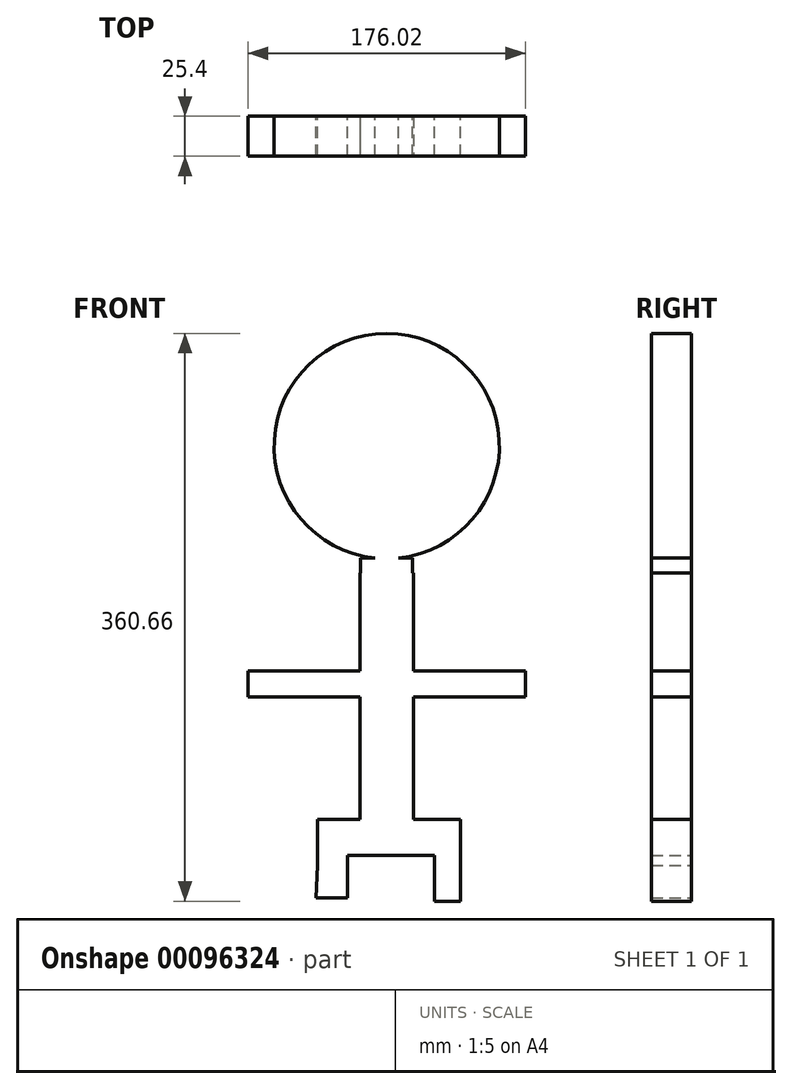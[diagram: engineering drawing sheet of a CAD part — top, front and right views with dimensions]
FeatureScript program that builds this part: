
annotation { "Feature Type Name" : "Feature", "Feature Type Description" : "" }
export const myFeature = defineFeature(function(context is Context, id is Id, definition is map)
    precondition{}
    {
        {
            var Q0;
            Q0=qCreatedBy(makeId("Front.planeOp"),FACE);
            var sketch = newSketch(context, id + "F0", { "sketchPlane" : qUnion([Q0])});
            skCircle(sketch, "E0", {"center": v(0, 0) * mm, "radius": 71.54 * mm});
            skSolve(sketch);
        }
        {
            var Q0;
            Q0=makeQuery(id+"F0.imprint","IMPRINT",FACE,{"disambiguationData":[TD([[makeQuery(id+"F0.imprint","IMPRINT",EDGE,{"derivedFrom":sQuery(id+"F0.wireOp",EDGE,"E0")}),1.0]])]});
            extrude(context, id + "F1", {"entities" : qUnion([Q0]), "depth" : 25.4 * mm});
        }
        {
            var Q0;
            Q0=qCreatedBy(makeId("Front.planeOp"),FACE);
            var sketch = newSketch(context, id + "F2", { "sketchPlane" : qUnion([Q0])});
            skCircle(sketch, "E1", {"center": v(-21.64, 37.84) * mm, "radius": 12.7 * mm});
            skCircle(sketch, "E2", {"center": v(21.64, 37.84) * mm, "radius": 12.7 * mm});
            skSolve(sketch);
        }
        {
            var Q0;
            Q0=sQuery(id+"F2.wireOp",EDGE,"E1");
            var Q1;
            Q1=sQuery(id+"F2.wireOp",EDGE,"E2");
            extrude(context, id + "F3", {"bodyType" : ToolBodyType.SURFACE, "surfaceEntities" : qUnion([Q0, Q1]), "depth" : 25.4 * mm});
        }
        {
            var Q0;
            Q0=qCreatedBy(makeId("Front.planeOp"),FACE);
            var sketch = newSketch(context, id + "F4", { "sketchPlane" : qUnion([Q0])});
            skLineSegment(sketch, "E3.bottom", {"start": v(0, -71.13) * mm, "end": v(-16.78, -71.13) * mm});
            skLineSegment(sketch, "E3.top", {"start": v(0, -145.62) * mm, "end": v(-16.78, -145.62) * mm});
            skLineSegment(sketch, "E3.left", {"start": v(0, -71.13) * mm, "end": v(0, -145.62) * mm});
            skLineSegment(sketch, "E3.right", {"start": v(-16.78, -71.13) * mm, "end": v(-16.78, -145.62) * mm});
            skLineSegment(sketch, "E4.bottom", {"start": v(0, -71.13) * mm, "end": v(16.43, -71.13) * mm});
            skLineSegment(sketch, "E4.top", {"start": v(0, -145.62) * mm, "end": v(16.43, -145.62) * mm});
            skLineSegment(sketch, "E4.right", {"start": v(16.43, -71.13) * mm, "end": v(16.43, -145.62) * mm});
            skSolve(sketch);
        }
        {
            var Q0;
            Q0=makeQuery(id+"F4.imprint","IMPRINT",FACE,{"disambiguationData":[TD([[makeQuery(id+"F4.imprint","IMPRINT",EDGE,{"derivedFrom":sQuery(id+"F4.wireOp",EDGE,"E3.bottom")}),1.0]])]});
            var Q1;
            Q1=makeQuery(id+"F4.imprint","IMPRINT",FACE,{"disambiguationData":[TD([[makeQuery(id+"F4.imprint","IMPRINT",EDGE,{"derivedFrom":sQuery(id+"F4.wireOp",EDGE,"E4.bottom")}),-1.0]])]});
            extrude(context, id + "F5", {"entities" : qUnion([Q0, Q1]), "operationType" : NewBodyOperationType.ADD, "depth" : 25.4 * mm});
        }
        {
            var Q0;
            Q0=qCreatedBy(makeId("Front.planeOp"),FACE);
            var sketch = newSketch(context, id + "F6", { "sketchPlane" : qUnion([Q0])});
            skLineSegment(sketch, "E5.bottom", {"start": v(-88, -159.3) * mm, "end": v(88, -159.3) * mm});
            skLineSegment(sketch, "E5.top", {"start": v(-88, -142.8) * mm, "end": v(88, -142.8) * mm});
            skLineSegment(sketch, "E5.left", {"start": v(-88, -159.3) * mm, "end": v(-88, -142.8) * mm});
            skLineSegment(sketch, "E5.right", {"start": v(88, -159.3) * mm, "end": v(88, -142.8) * mm});
            skPoint(sketch, "E5.middle", {"position": v(0, -151.06) * mm});
            skSolve(sketch);
        }
        {
            var Q0;
            Q0=makeQuery(id+"F6.imprint","IMPRINT",FACE,{"disambiguationData":[TD([[makeQuery(id+"F6.imprint","IMPRINT",EDGE,{"derivedFrom":sQuery(id+"F6.wireOp",EDGE,"E5.bottom")}),1.0]])]});
            extrude(context, id + "F7", {"entities" : qUnion([Q0]), "operationType" : NewBodyOperationType.ADD, "depth" : 25.4 * mm});
        }
        {
            var Q0;
            Q0=qCreatedBy(makeId("Front.planeOp"),FACE);
            var sketch = newSketch(context, id + "F8", { "sketchPlane" : qUnion([Q0])});
            skLineSegment(sketch, "E6.bottom", {"start": v(16.95, -237.23) * mm, "end": v(-16.95, -237.23) * mm});
            skLineSegment(sketch, "E6.top", {"start": v(16.95, -80.76) * mm, "end": v(-16.95, -80.76) * mm});
            skLineSegment(sketch, "E6.left", {"start": v(16.95, -237.23) * mm, "end": v(16.95, -80.76) * mm});
            skLineSegment(sketch, "E6.right", {"start": v(-16.95, -237.23) * mm, "end": v(-16.95, -80.76) * mm});
            skPoint(sketch, "E6.middle", {"position": v(0, -159) * mm});
            skSolve(sketch);
        }
        {
            var Q0;
            Q0=makeQuery(id+"F8.imprint","IMPRINT",FACE,{"disambiguationData":[TD([[makeQuery(id+"F8.imprint","IMPRINT",EDGE,{"derivedFrom":sQuery(id+"F8.wireOp",EDGE,"E6.bottom")}),-1.0]])]});
            extrude(context, id + "F9", {"entities" : qUnion([Q0]), "operationType" : NewBodyOperationType.ADD, "depth" : 25.4 * mm});
        }
        {
            var Q0;
            Q0=qCreatedBy(makeId("Front.planeOp"),FACE);
            var sketch = newSketch(context, id + "F10", { "sketchPlane" : qUnion([Q0])});
            skLineSegment(sketch, "E7", {"start": v(0, -237) * mm, "end": v(-43.94, -237) * mm});
            skLineSegment(sketch, "E8", {"start": v(-43.94, -237) * mm, "end": v(46.73, -237) * mm});
            skLineSegment(sketch, "E9", {"start": v(46.73, -237) * mm, "end": v(46.73, -289.12) * mm});
            skLineSegment(sketch, "E10", {"start": v(46.73, -289.12) * mm, "end": v(30.45, -289.12) * mm});
            skLineSegment(sketch, "E11", {"start": v(30.45, -289.12) * mm, "end": v(30.45, -259.99) * mm});
            skLineSegment(sketch, "E12", {"start": v(30.45, -259.99) * mm, "end": v(-25.03, -259.99) * mm});
            skLineSegment(sketch, "E13", {"start": v(-25.03, -259.99) * mm, "end": v(-25.03, -287.05) * mm});
            skLineSegment(sketch, "E14", {"start": v(-25.03, -287.05) * mm, "end": v(-44.81, -287.05) * mm});
            skLineSegment(sketch, "E15", {"start": v(-43.94, -266.22) * mm, "end": v(-44.81, -287.05) * mm});
            skLineSegment(sketch, "E16", {"start": v(-43.94, -266.22) * mm, "end": v(-43.94, -237) * mm});
            skSolve(sketch);
        }
        {
            var Q0;
            {var subQ1=sQuery(id+"F10.wireOp",EDGE,"E9");Q0=makeQuery(id+"F10.imprint","IMPRINT",FACE,{"disambiguationData":[TD([[makeQuery(id+"F10.imprint","IMPRINT",EDGE,{"derivedFrom":subQ1}),-1.0]])]});}
            extrude(context, id + "F11", {"entities" : qUnion([Q0]), "operationType" : NewBodyOperationType.ADD, "depth" : 25.4 * mm});
        }
    });
